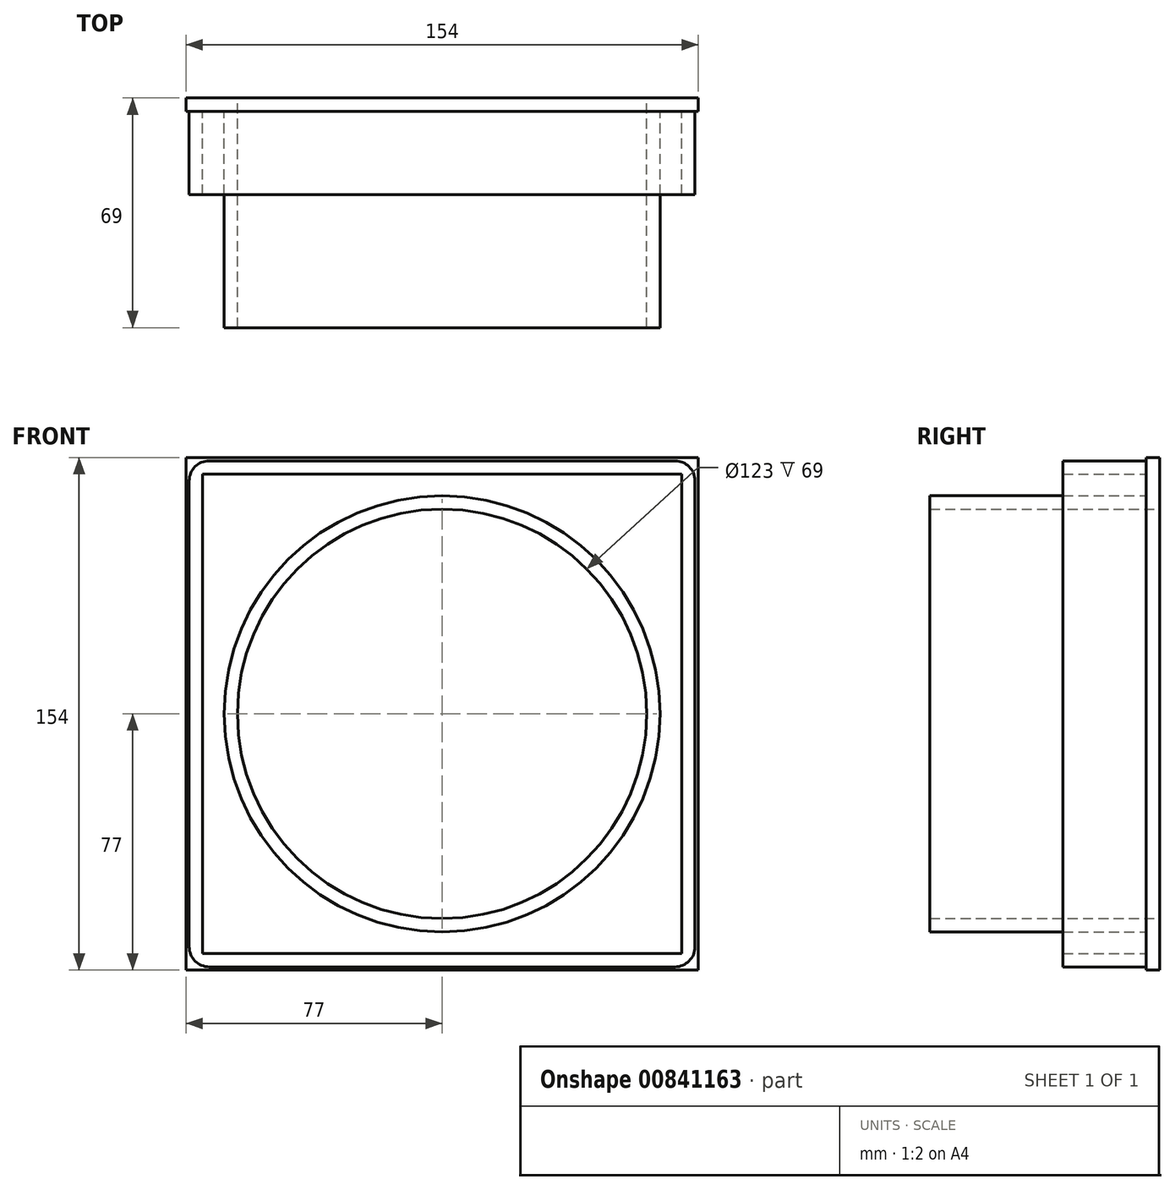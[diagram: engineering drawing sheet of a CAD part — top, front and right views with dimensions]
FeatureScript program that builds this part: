
annotation { "Feature Type Name" : "Feature", "Feature Type Description" : "" }
export const myFeature = defineFeature(function(context is Context, id is Id, definition is map)
    precondition{}
    {
        {
            var Q0;
            Q0=qCreatedBy(makeId("Front.planeOp"),FACE);
            var sketch = newSketch(context, id + "F0", { "sketchPlane" : qUnion([Q0])});
            skLineSegment(sketch, "E0.bottom", {"start": v(77, -77) * mm, "end": v(-77, -77) * mm});
            skLineSegment(sketch, "E0.top", {"start": v(77, 77) * mm, "end": v(-77, 77) * mm});
            skLineSegment(sketch, "E0.left", {"start": v(77, -77) * mm, "end": v(77, 77) * mm});
            skLineSegment(sketch, "E0.right", {"start": v(-77, -77) * mm, "end": v(-77, 77) * mm});
            skPoint(sketch, "E0.middle", {"position": v(0, 0) * mm});
            skSolve(sketch);
        }
        {
            var Q0;
            Q0=makeQuery(id+"F0.imprint","IMPRINT",FACE,{"disambiguationData":[TD([[makeQuery(id+"F0.imprint","IMPRINT",EDGE,{"derivedFrom":sQuery(id+"F0.wireOp",EDGE,"E0.bottom")}),-1.0]])]});
            extrude(context, id + "F1", {"entities" : qUnion([Q0]), "oppositeDirection" : true, "depth" : 4 * mm, "offsetDistance" : 25 * mm});
        }
        {
            var Q0;
            Q0=makeQuery(id+"F1.opExtrude","CAP_FACE",FACE,{"disambiguationData":[OSD([sQuery(id+"F0.wireOp",EDGE,"E0.bottom"),sQuery(id+"F0.wireOp",EDGE,"E0.top"),sQuery(id+"F0.wireOp",EDGE,"E0.left"),sQuery(id+"F0.wireOp",EDGE,"E0.right")])],"isStart":true});
            var sketch = newSketch(context, id + "F2", { "sketchPlane" : qUnion([Q0])});
            skLineSegment(sketch, "E1.bottom", {"start": v(-70, -76) * mm, "end": v(70, -76) * mm});
            skLineSegment(sketch, "E1.top", {"start": v(-70, 76) * mm, "end": v(70, 76) * mm});
            skLineSegment(sketch, "E1.left", {"start": v(-76, -70) * mm, "end": v(-76, 70) * mm});
            skLineSegment(sketch, "E1.right", {"start": v(76, -70) * mm, "end": v(76, 70) * mm});
            skPoint(sketch, "E1.middle", {"position": v(0, 0) * mm});
            skPoint(sketch, "E2.visualSharp", {"position": v(-76, 76) * mm});
            skArc(sketch, "E2.filletArc", {"start": v(-70, 76) * mm, "mid": v(-74.24, 74.24) * mm, "end": v(-76, 70) * mm});
            skPoint(sketch, "E3.visualSharp", {"position": v(76, 76) * mm});
            skArc(sketch, "E3.filletArc", {"start": v(76, 70) * mm, "mid": v(74.24, 74.24) * mm, "end": v(70, 76) * mm});
            skPoint(sketch, "E4.visualSharp", {"position": v(76, -76) * mm});
            skArc(sketch, "E4.filletArc", {"start": v(70, -76) * mm, "mid": v(74.24, -74.24) * mm, "end": v(76, -70) * mm});
            skPoint(sketch, "E5.visualSharp", {"position": v(-76, -76) * mm});
            skArc(sketch, "E5.filletArc", {"start": v(-76, -70) * mm, "mid": v(-74.24, -74.24) * mm, "end": v(-70, -76) * mm});
            skArc(sketch, "E6.0", {"start": v(-70, 72) * mm, "mid": v(-71.41, 71.41) * mm, "end": v(-72, 70) * mm});
            skLineSegment(sketch, "E6.1", {"start": v(-72, -70) * mm, "end": v(-72, 70) * mm});
            skLineSegment(sketch, "E6.2", {"start": v(-70, 72) * mm, "end": v(70, 72) * mm});
            skArc(sketch, "E6.3", {"start": v(-72, -70) * mm, "mid": v(-71.41, -71.41) * mm, "end": v(-70, -72) * mm});
            skArc(sketch, "E6.4", {"start": v(72, 70) * mm, "mid": v(71.41, 71.41) * mm, "end": v(70, 72) * mm});
            skLineSegment(sketch, "E6.5", {"start": v(72, -70) * mm, "end": v(72, 70) * mm});
            skArc(sketch, "E6.6", {"start": v(70, -72) * mm, "mid": v(71.41, -71.41) * mm, "end": v(72, -70) * mm});
            skLineSegment(sketch, "E6.7", {"start": v(-70, -72) * mm, "end": v(70, -72) * mm});
            skLineSegment(sketch, "E7.0", {"start": v(72, -72) * mm, "end": v(72, 72) * mm});
            skLineSegment(sketch, "E7.1", {"start": v(-72, -72) * mm, "end": v(72, -72) * mm});
            skLineSegment(sketch, "E7.2", {"start": v(-72, 72) * mm, "end": v(-72, -72) * mm});
            skLineSegment(sketch, "E7.3", {"start": v(72, 72) * mm, "end": v(-72, 72) * mm});
            skSolve(sketch);
        }
        {
            var Q0;
            Q0=makeQuery(id+"F2.imprint","IMPRINT",FACE,{"disambiguationData":[TD([[makeQuery(id+"F2.imprint","IMPRINT",EDGE,{"derivedFrom":sQuery(id+"F2.wireOp",EDGE,"E1.bottom")}),1.0]])]});
            extrude(context, id + "F3", {"entities" : qUnion([Q0]), "operationType" : NewBodyOperationType.ADD, "depth" : 25 * mm, "offsetDistance" : 25 * mm});
        }
        {
            var Q0;
            Q0=makeQuery(id+"F3.boolean.opBoolean","SPLIT",FACE,{"disambiguationData":[TD([makeQuery(id+"F3.opExtrude","SWEPT_FACE",FACE,{"disambiguationData":[OSD([sQuery(id+"F2.wireOp",EDGE,"E7.0")])]})])],"derivedFrom":makeQuery(id+"F1.opExtrude","CAP_FACE",FACE,{"disambiguationData":[OSD([sQuery(id+"F0.wireOp",EDGE,"E0.bottom"),sQuery(id+"F0.wireOp",EDGE,"E0.top"),sQuery(id+"F0.wireOp",EDGE,"E0.left"),sQuery(id+"F0.wireOp",EDGE,"E0.right")])],"isStart":true})});
            var sketch = newSketch(context, id + "F4", { "sketchPlane" : qUnion([Q0])});
            skCircle(sketch, "E8", {"center": v(0, 0) * mm, "radius": 61.5 * mm});
            skCircle(sketch, "E9.0", {"center": v(0, 0) * mm, "radius": 65.5 * mm});
            skLineSegment(sketch, "E10.0", {"start": v(77, 77) * mm, "end": v(-77, 77) * mm});
            skLineSegment(sketch, "E10.1", {"start": v(77, -77) * mm, "end": v(77, 77) * mm});
            skLineSegment(sketch, "E10.2", {"start": v(-77, -77) * mm, "end": v(77, -77) * mm});
            skLineSegment(sketch, "E10.3", {"start": v(-77, 77) * mm, "end": v(-77, -77) * mm});
            skSolve(sketch);
        }
        {
            var Q0;
            Q0=makeQuery(id+"F4.imprint","IMPRINT",FACE,{"disambiguationData":[TD([[makeQuery(id+"F4.imprint","IMPRINT",EDGE,{"derivedFrom":sQuery(id+"F4.wireOp",EDGE,"E8")}),-1.0]])]});
            extrude(context, id + "F5", {"entities" : qUnion([Q0]), "operationType" : NewBodyOperationType.ADD, "depth" : 65 * mm, "offsetDistance" : 25 * mm});
        }
        {
            var Q0;
            Q0=makeQuery(id+"F5.boolean.opBoolean","SPLIT",FACE,{"disambiguationData":[TD([makeQuery(id+"F5.opExtrude","SWEPT_FACE",FACE,{"disambiguationData":[OSD([sQuery(id+"F4.wireOp",EDGE,"E8")])]})])],"derivedFrom":makeQuery(id+"F3.boolean.opBoolean","SPLIT",FACE,{"disambiguationData":[TD([makeQuery(id+"F3.opExtrude","SWEPT_FACE",FACE,{"disambiguationData":[OSD([sQuery(id+"F2.wireOp",EDGE,"E7.0")])]})])],"derivedFrom":makeQuery(id+"F1.opExtrude","CAP_FACE",FACE,{"disambiguationData":[OSD([sQuery(id+"F0.wireOp",EDGE,"E0.bottom"),sQuery(id+"F0.wireOp",EDGE,"E0.top"),sQuery(id+"F0.wireOp",EDGE,"E0.left"),sQuery(id+"F0.wireOp",EDGE,"E0.right")])],"isStart":true})})});
            extrude(context, id + "F6", {"entities" : qUnion([Q0]), "operationType" : NewBodyOperationType.REMOVE, "oppositeDirection" : true, "depth" : 88.2 * mm, "offsetDistance" : 25 * mm});
        }
    });
